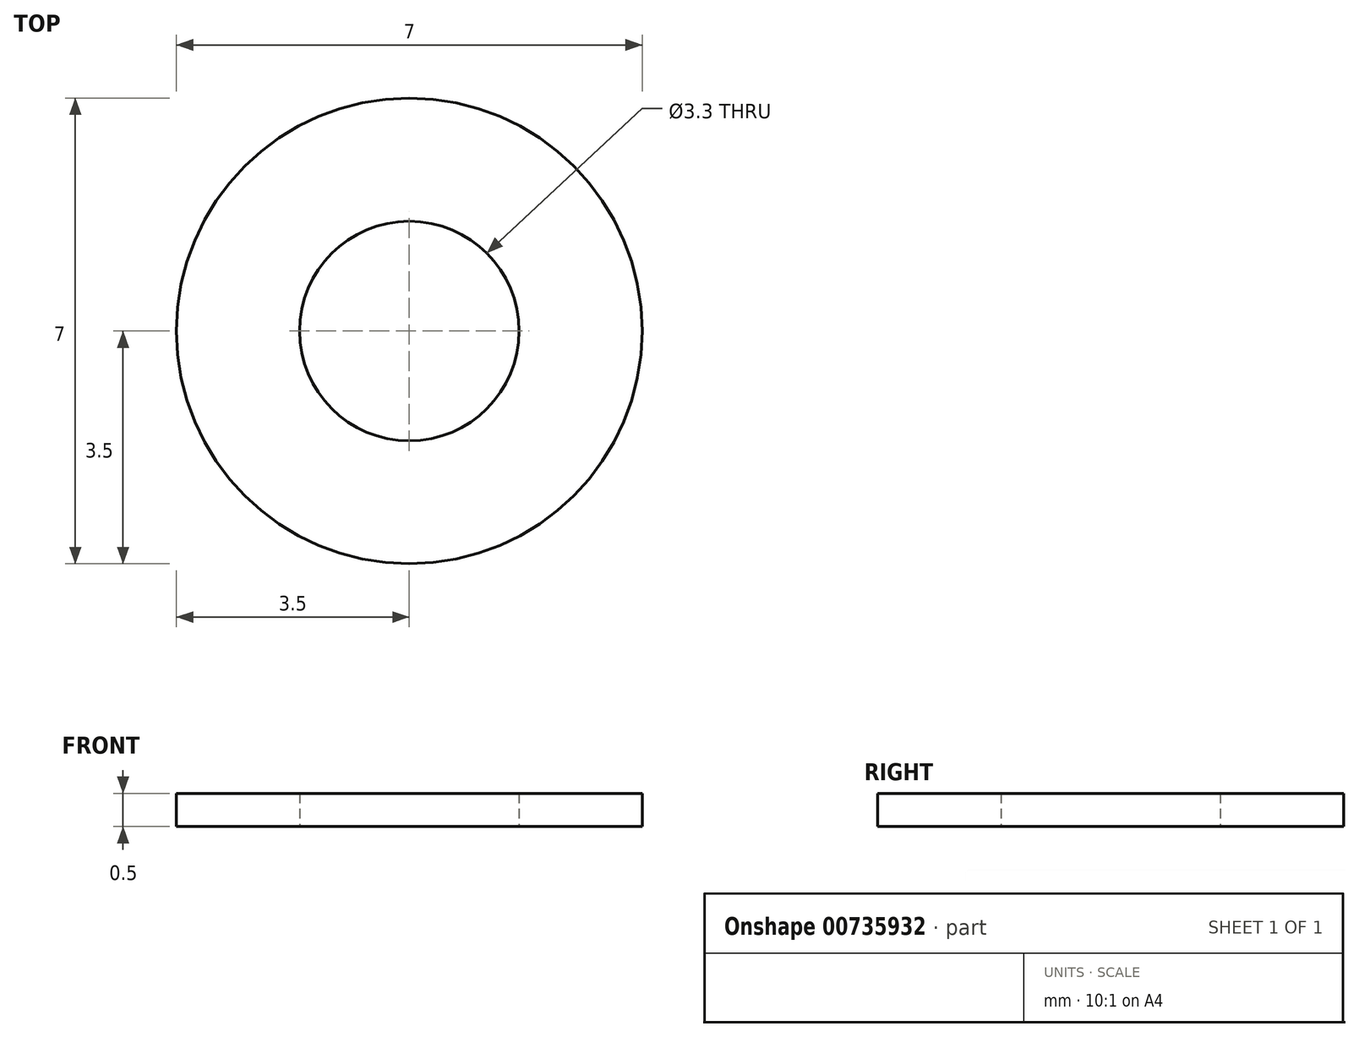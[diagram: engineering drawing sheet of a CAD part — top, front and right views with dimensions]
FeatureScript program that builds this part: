
annotation { "Feature Type Name" : "Feature", "Feature Type Description" : "" }
export const myFeature = defineFeature(function(context is Context, id is Id, definition is map)
    precondition{}
    {
        {
            var Q0;
            Q0=qCreatedBy(makeId("Top.planeOp"),FACE);
            var sketch = newSketch(context, id + "F0", { "sketchPlane" : qUnion([Q0])});
            skCircle(sketch, "E0", {"center": v(0, 0) * mm, "radius": 3.5 * mm});
            skCircle(sketch, "E1", {"center": v(0, 0) * mm, "radius": 1.65 * mm});
            skSolve(sketch);
        }
        {
            var Q0;
            Q0=makeQuery(id+"F0.imprint","IMPRINT",FACE,{"disambiguationData":[TD([[makeQuery(id+"F0.imprint","IMPRINT",EDGE,{"derivedFrom":sQuery(id+"F0.wireOp",EDGE,"E0")}),1.0]])]});
            extrude(context, id + "F1", {"entities" : qUnion([Q0]), "depth" : 0.5 * mm, "offsetDistance" : 25 * mm});
        }
    });
